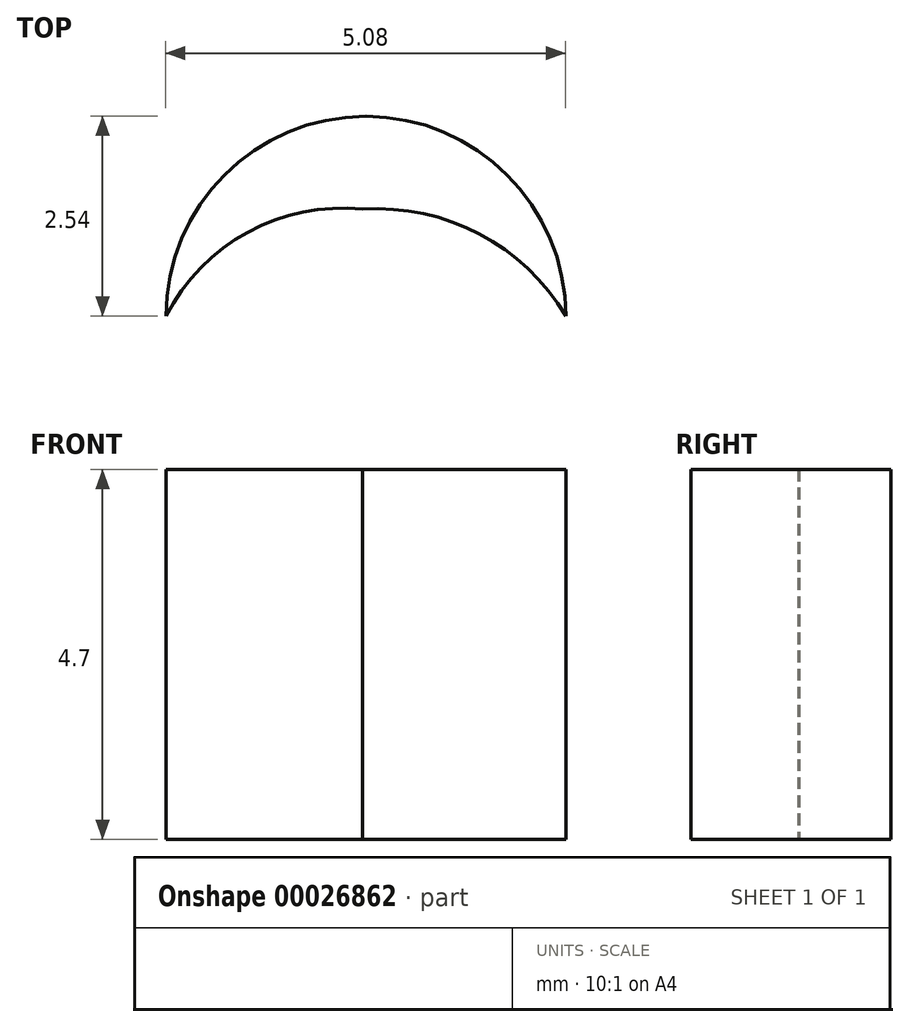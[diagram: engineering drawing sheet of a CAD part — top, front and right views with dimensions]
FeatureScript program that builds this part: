
annotation { "Feature Type Name" : "Feature", "Feature Type Description" : "" }
export const myFeature = defineFeature(function(context is Context, id is Id, definition is map)
    precondition{}
    {
        {
            var Q0;
            Q0=qCreatedBy(makeId("Top.planeOp"),FACE);
            var sketch = newSketch(context, id + "F0", { "sketchPlane" : qUnion([Q0])});
            skArc(sketch, "E0", {"start": v(-299.04, 251.93) * mm, "mid": v(-301.58, 254.47) * mm, "end": v(-304.12, 251.93) * mm});
            skLineSegment(sketch, "E1", {"start": v(-301.58, 251.93) * mm, "end": v(-301.59, 251.93) * mm});
            skLineSegment(sketch, "E2", {"start": v(-304.12, 251.93) * mm, "end": v(-304.1, 251.93) * mm});
            skArc(sketch, "E3", {"start": v(-304.1, 251.95) * mm, "mid": v(-304.1, 251.94) * mm, "end": v(-304.1, 251.93) * mm});
            skArc(sketch, "E4", {"start": v(-301.62, 253.29) * mm, "mid": v(-303.08, 253) * mm, "end": v(-304.12, 251.93) * mm});
            skArc(sketch, "E5", {"start": v(-299.04, 251.93) * mm, "mid": v(-300.13, 252.97) * mm, "end": v(-301.62, 253.29) * mm});
            skLineSegment(sketch, "E6.trimOffspring", {"start": v(-301.59, 251.93) * mm, "end": v(-301.58, 251.93) * mm});
            skLineSegment(sketch, "E7.trimOffspring", {"start": v(-304.1, 251.93) * mm, "end": v(-304.12, 251.93) * mm});
            skPoint(sketch, "E8.center.orphan", {"position": v(-300.3, 251.93) * mm});
            skSolve(sketch);
        }
        {
            var Q0;
            {var subQ3=sQuery(id+"F0.wireOp",EDGE,"E0");Q0=makeQuery(id+"F0.imprint","IMPRINT",FACE,{"disambiguationData":[TD([[makeQuery(id+"F0.imprint","IMPRINT",EDGE,{"derivedFrom":subQ3}),1.0]])]});}
            extrude(context, id + "F1", {"entities" : qUnion([Q0]), "depth" : 4.7 * mm});
        }
    });
